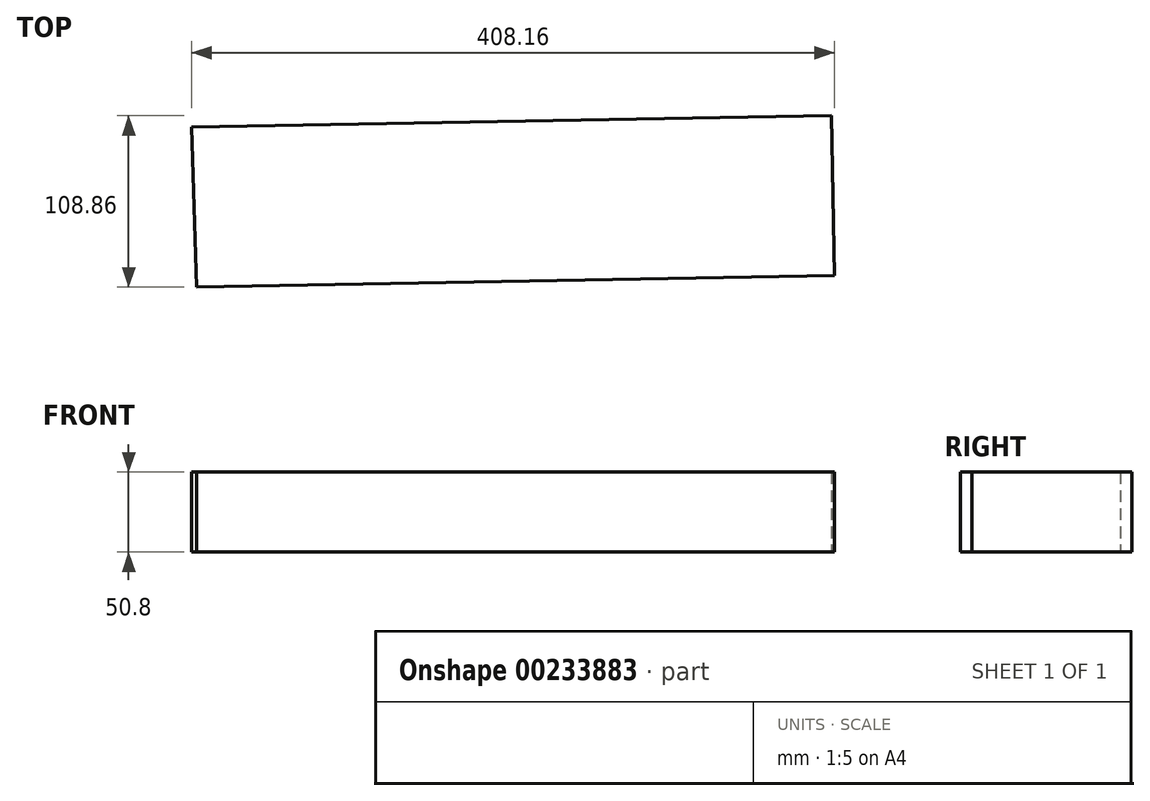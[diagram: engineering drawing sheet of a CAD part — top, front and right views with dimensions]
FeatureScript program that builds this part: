
annotation { "Feature Type Name" : "Feature", "Feature Type Description" : "" }
export const myFeature = defineFeature(function(context is Context, id is Id, definition is map)
    precondition{}
    {
        {
            var Q0;
            Q0=qCreatedBy(makeId("Top.planeOp"),FACE);
            var sketch = newSketch(context, id + "F0", { "sketchPlane" : qUnion([Q0])});
            skLineSegment(sketch, "E0", {"start": v(-85.72, 40.9) * mm, "end": v(320.61, 48.2) * mm});
            skLineSegment(sketch, "E1", {"start": v(320.61, 48.2) * mm, "end": v(322.44, -53.37) * mm});
            skLineSegment(sketch, "E2", {"start": v(322.44, -53.37) * mm, "end": v(-82.75, -60.66) * mm});
            skLineSegment(sketch, "E3", {"start": v(-82.75, -60.66) * mm, "end": v(-85.72, 40.9) * mm});
            skSolve(sketch);
        }
        {
            var Q0;
            Q0=makeQuery(id+"F0.imprint","IMPRINT",FACE,{"disambiguationData":[TD([[makeQuery(id+"F0.imprint","IMPRINT",EDGE,{"derivedFrom":sQuery(id+"F0.wireOp",EDGE,"E0")}),-1.0]])]});
            extrude(context, id + "F1", {"entities" : qUnion([Q0]), "depth" : 50.8 * mm});
        }
    });
